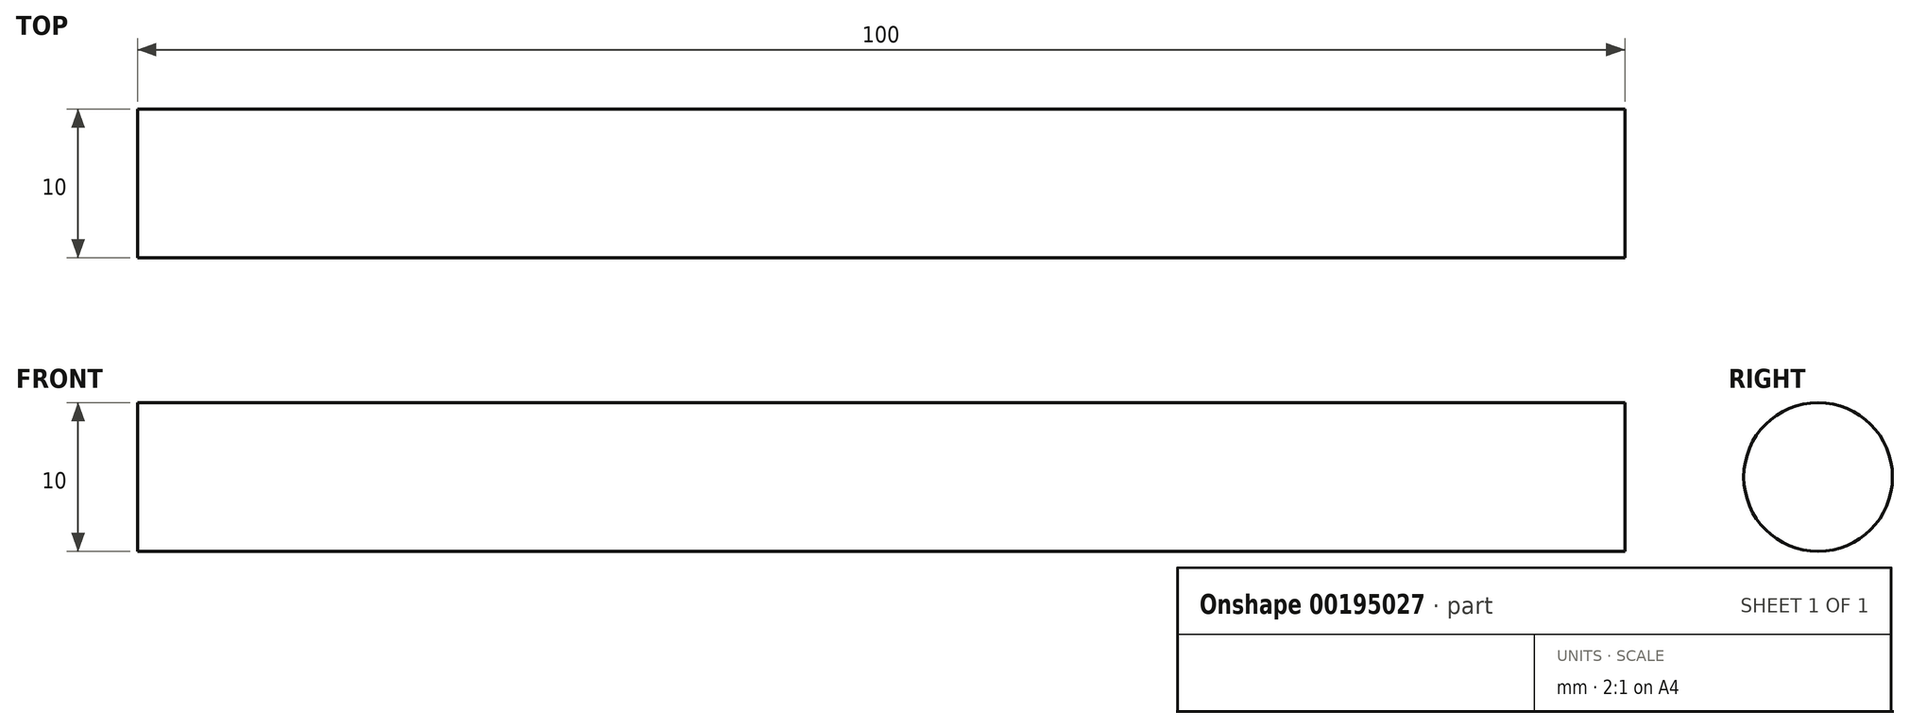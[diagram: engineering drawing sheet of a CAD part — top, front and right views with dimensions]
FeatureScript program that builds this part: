
annotation { "Feature Type Name" : "Feature", "Feature Type Description" : "" }
export const myFeature = defineFeature(function(context is Context, id is Id, definition is map)
    precondition{}
    {
        {
            var Q0;
            Q0=qCreatedBy(makeId("Top.planeOp"),FACE);
            var sketch = newSketch(context, id + "F0", { "sketchPlane" : qUnion([Q0])});
            skLineSegment(sketch, "E0", {"start": v(-65.77, 0) * mm, "end": v(-65.77, 5) * mm});
            skLineSegment(sketch, "E1", {"start": v(-65.77, 5) * mm, "end": v(34.23, 5) * mm});
            skLineSegment(sketch, "E2", {"start": v(34.23, 5) * mm, "end": v(34.23, 0) * mm});
            skLineSegment(sketch, "E3", {"start": v(34.23, 0) * mm, "end": v(-65.77, 0) * mm});
            skSolve(sketch);
        }
        {
            var Q0;
            Q0=makeQuery(id+"F0.imprint","IMPRINT",FACE,{"disambiguationData":[TD([[makeQuery(id+"F0.imprint","IMPRINT",EDGE,{"derivedFrom":sQuery(id+"F0.wireOp",EDGE,"E0")}),-1.0]])]});
            var Q1;
            Q1=sQuery(id+"F0.wireOp",EDGE,"E3");
            revolve(context, id + "F1", {"entities" : qUnion([Q0]), "axis" : qUnion([Q1]), "revolveType" : RevolveType.FULL});
        }
    });
